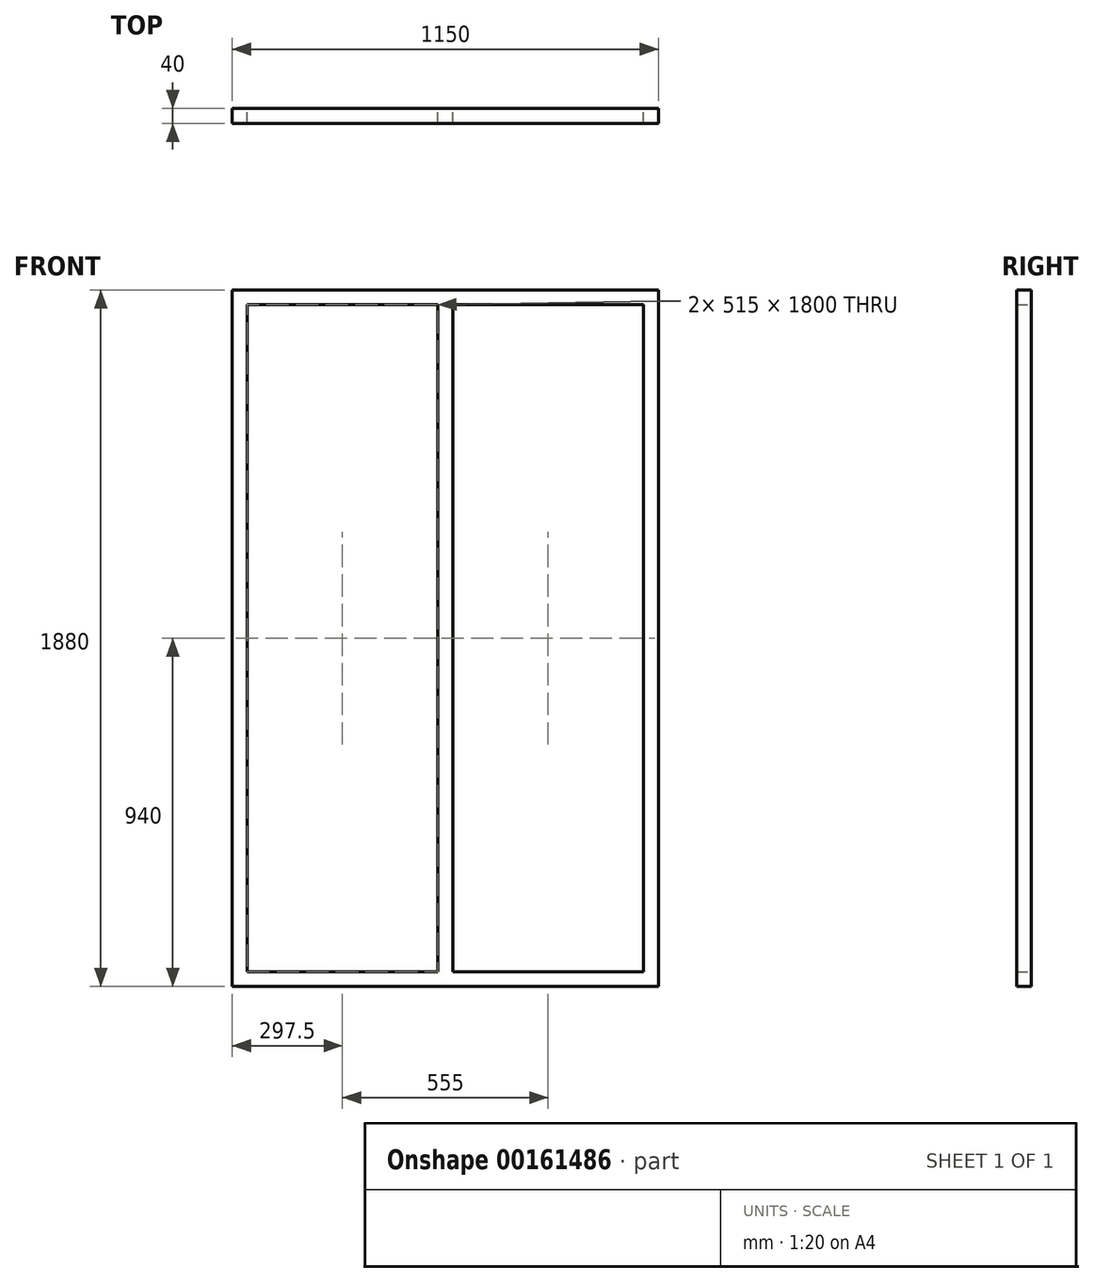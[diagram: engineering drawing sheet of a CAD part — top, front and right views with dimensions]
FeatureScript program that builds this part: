
annotation { "Feature Type Name" : "Feature", "Feature Type Description" : "" }
export const myFeature = defineFeature(function(context is Context, id is Id, definition is map)
    precondition{}
    {
        {
            var Q0;
            Q0=qCreatedBy(makeId("Front.planeOp"),FACE);
            var sketch = newSketch(context, id + "F0", { "sketchPlane" : qUnion([Q0])});
            skLineSegment(sketch, "E0.bottom", {"start": v(-535, 900) * mm, "end": v(-20, 900) * mm});
            skLineSegment(sketch, "E0.top", {"start": v(-535, -900) * mm, "end": v(-20, -900) * mm});
            skLineSegment(sketch, "E0.left", {"start": v(-535, 900) * mm, "end": v(-535, -900) * mm});
            skLineSegment(sketch, "E0.right", {"start": v(535, 900) * mm, "end": v(535, -900) * mm});
            skPoint(sketch, "E0.middle", {"position": v(0, 0) * mm});
            skLineSegment(sketch, "E1.bottom", {"start": v(-575, 940) * mm, "end": v(575, 940) * mm});
            skLineSegment(sketch, "E1.top", {"start": v(-575, -940) * mm, "end": v(575, -940) * mm});
            skLineSegment(sketch, "E1.left", {"start": v(-575, 940) * mm, "end": v(-575, -940) * mm});
            skLineSegment(sketch, "E1.right", {"start": v(575, 940) * mm, "end": v(575, -940) * mm});
            skLineSegment(sketch, "E2.left", {"start": v(-20, 900) * mm, "end": v(-20, -900) * mm});
            skLineSegment(sketch, "E2.right", {"start": v(20, 900) * mm, "end": v(20, -900) * mm});
            skLineSegment(sketch, "E3.trimOffspring", {"start": v(20, -900) * mm, "end": v(535, -900) * mm});
            skLineSegment(sketch, "E4.trimOffspring", {"start": v(20, 900) * mm, "end": v(535, 900) * mm});
            skSolve(sketch);
        }
        {
            var Q0;
            Q0 = qSketchRegion(id + "F0", true);
            extrude(context, id + "F1", {"entities" : qUnion([Q0]), "endBound" : BoundingType.SYMMETRIC, "depth" : 40 * mm, "offsetDistance" : 25 * mm});
        }
    });
